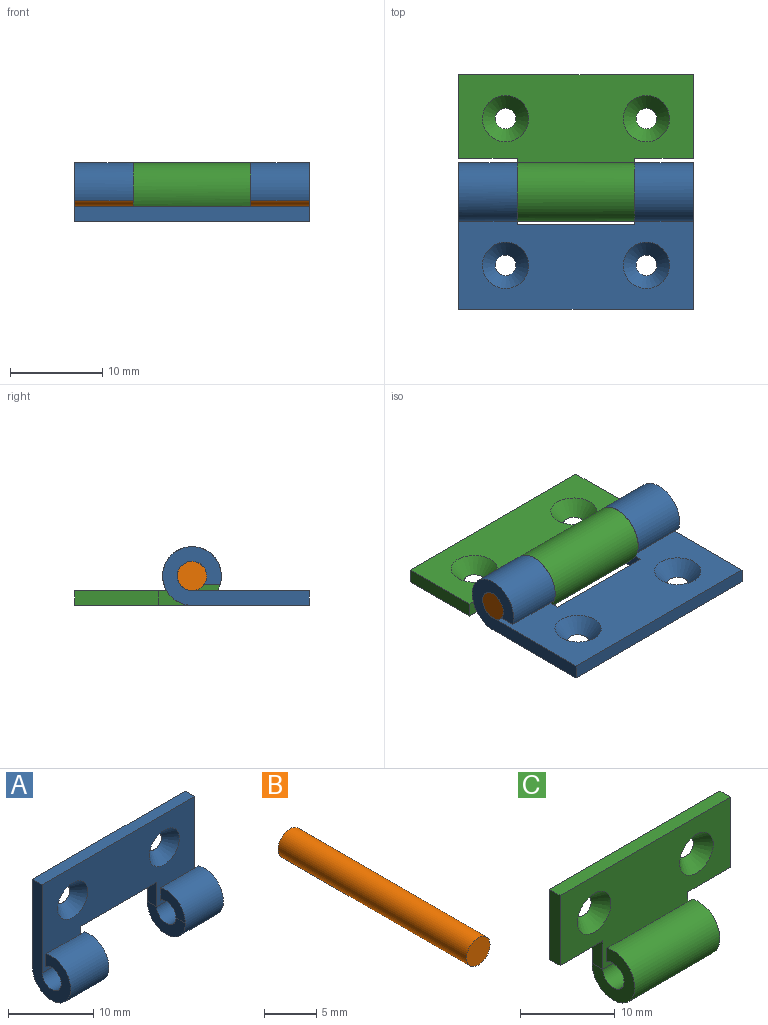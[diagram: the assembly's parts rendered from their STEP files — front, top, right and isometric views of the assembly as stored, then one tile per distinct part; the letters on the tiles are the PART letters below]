
ASSEMBLY  parts=3 mates=2
PART A: 19 faces, bbox 25.4x6.4x15.9 mm
  f0: plane 25.4x12.71mm, normal (0,-1,0), area 238.8mm2, adj f3,f5,f7,f8,f9,f10,f11,f16
  f1: plane 25.4x12.71mm, normal (0,1,0), area 270.1mm2, adj f2,f5,f6,f7,f8,f9,f10,f16
  f2: cylinder r=3.17mm len=6.35mm, axis (-1,0,0), area 101mm2, adj f1,f4,f8,f13,f15
  f3: cylinder r=1.59mm len=6.35mm, axis (-1,0,0), area 53.9mm2, adj f0,f4,f8,f13,f15
  f4: plane 6.34x1.76mm, normal (0,1,0), area 11.2mm2, adj f2,f3,f8,f15
  f5: plane 15.88x6.35mm, normal (-1,0,0), area 39.5mm2, adj f0,f1,f6,f7,f11,f12
  f6: cylinder r=3.17mm len=6.35mm, axis (-1,0,0), area 101.2mm2, adj f1,f5,f12,f14
  f7: plane 25.4x1.59mm, normal (0,0,1), area 40.3mm2, adj f0,f1,f5,f8
  f8: plane 15.88x6.35mm, normal (1,0,0), area 39.5mm2, adj f0,f1,f2,f3,f4,f7
  f9: cone r=0.89mm half-angle=41deg, axis (0,-1,0), area 23.9mm2, adj f0,f1
  f10: cone r=0.89mm half-angle=41deg, axis (0,-1,0), area 23.9mm2, adj f0,f1
  f11: cylinder r=1.59mm len=6.35mm, axis (-1,0,0), area 54mm2, adj f0,f5,f12,f14
  f12: plane 6.35x1.76mm, normal (0,1,0), area 11.2mm2, adj f5,f6,f11,f14
  f13: plane 6.36x3.19mm, normal (-1,0,0), area 11.9mm2, adj f2,f3,f15,f18
  f14: plane 6.35x6.35mm, normal (1,0,0), area 19.4mm2, adj f6,f11,f12,f17
  f15: plane 4.14x3.19mm, normal (-1,0,0), area 7.5mm2, adj f2,f3,f4,f13
  f16: plane 12.7x1.59mm, normal (0,0,-1), area 20.2mm2, adj f0,f1,f17,f18
  f17: plane 3.52x1.59mm, normal (1,0,0), area 5.6mm2, adj f0,f1,f14,f16
  f18: plane 3.52x1.6mm, normal (-1,0,0), area 5.6mm2, adj f0,f1,f13,f16
PART B: 3 faces, bbox 3.2x25.4x3.2 mm
  f0: cylinder r=1.59mm len=25.4mm, axis (0,1,0), area 253.4mm2, adj f1,f2
  f1: plane 3.18x3.18mm, normal (0,-1,0), area 7.9mm2, adj f0
  f2: plane 3.18x3.18mm, normal (0,1,0), area 7.9mm2, adj f0
PART C: 17 faces, bbox 25.4x6.4x15.9 mm
  f0: plane 9.04x1.59mm, normal (-1,0,0), area 14.3mm2, adj f5,f6,f7,f13
  f1: cylinder r=3.17mm len=12.71mm, axis (-1,0,0), area 202.4mm2, adj f3,f7,f10,f11,f12
  f2: cylinder r=1.59mm len=12.71mm, axis (-1,0,0), area 108mm2, adj f3,f6,f10,f11,f12
  f3: plane 12.7x1.76mm, normal (0,1,0), area 22.3mm2, adj f1,f2,f10,f12
  f4: plane 9.04x1.59mm, normal (1,0,0), area 14.3mm2, adj f5,f6,f7,f16
  f5: plane 25.4x1.59mm, normal (0,0,1), area 40.3mm2, adj f0,f4,f6,f7
  f6: plane 25.4x12.7mm, normal (0,-1,0), area 236.8mm2, adj f0,f2,f4,f5,f8,f9,f13,f14
  f7: plane 25.4x12.7mm, normal (0,1,0), area 268.2mm2, adj f0,f1,f4,f5,f8,f9,f13,f14
  f8: cone r=0.89mm half-angle=41deg, axis (0,-1,0), area 23.9mm2, adj f6,f7
  f9: cone r=0.89mm half-angle=41deg, axis (0,-1,0), area 23.9mm2, adj f6,f7
  f10: plane 6.36x6.36mm, normal (-1,0,0), area 19.4mm2, adj f1,f2,f3,f14
  f11: plane 6.36x3.18mm, normal (1,0,0), area 11.9mm2, adj f1,f2,f12,f15
  f12: plane 4.14x3.18mm, normal (1,0,0), area 7.5mm2, adj f1,f2,f3,f11
  f13: plane 6.35x1.59mm, normal (0,0,-1), area 10.1mm2, adj f0,f6,f7,f14
  f14: plane 3.67x1.59mm, normal (-1,0,0), area 5.8mm2, adj f6,f7,f10,f13
  f15: plane 3.67x1.59mm, normal (1,0,0), area 5.8mm2, adj f6,f7,f11,f16
  f16: plane 6.35x1.59mm, normal (0,0,-1), area 10.1mm2, adj f4,f6,f7,f15
PLACE A rot(axis=(0,-0.71,0.71),180deg) t=(-69.62,8.89,-3.14)mm
PLACE B rot(axis=(-0.71,0.71,0),180deg) t=(-42.32,-69.9,51.73)mm
PLACE C rot(axis=(-1,0,0),90deg) t=(10.38,-27.29,-3.14)mm
MATE cylindrical B.f0 <-> A.f2  axis (-1,0,0) through (-16.92,-9.2,0.04)mm
MATE cylindrical B.f0 <-> C.f1  axis (-1,0,0) through (-29.62,-9.2,0.04)mm
